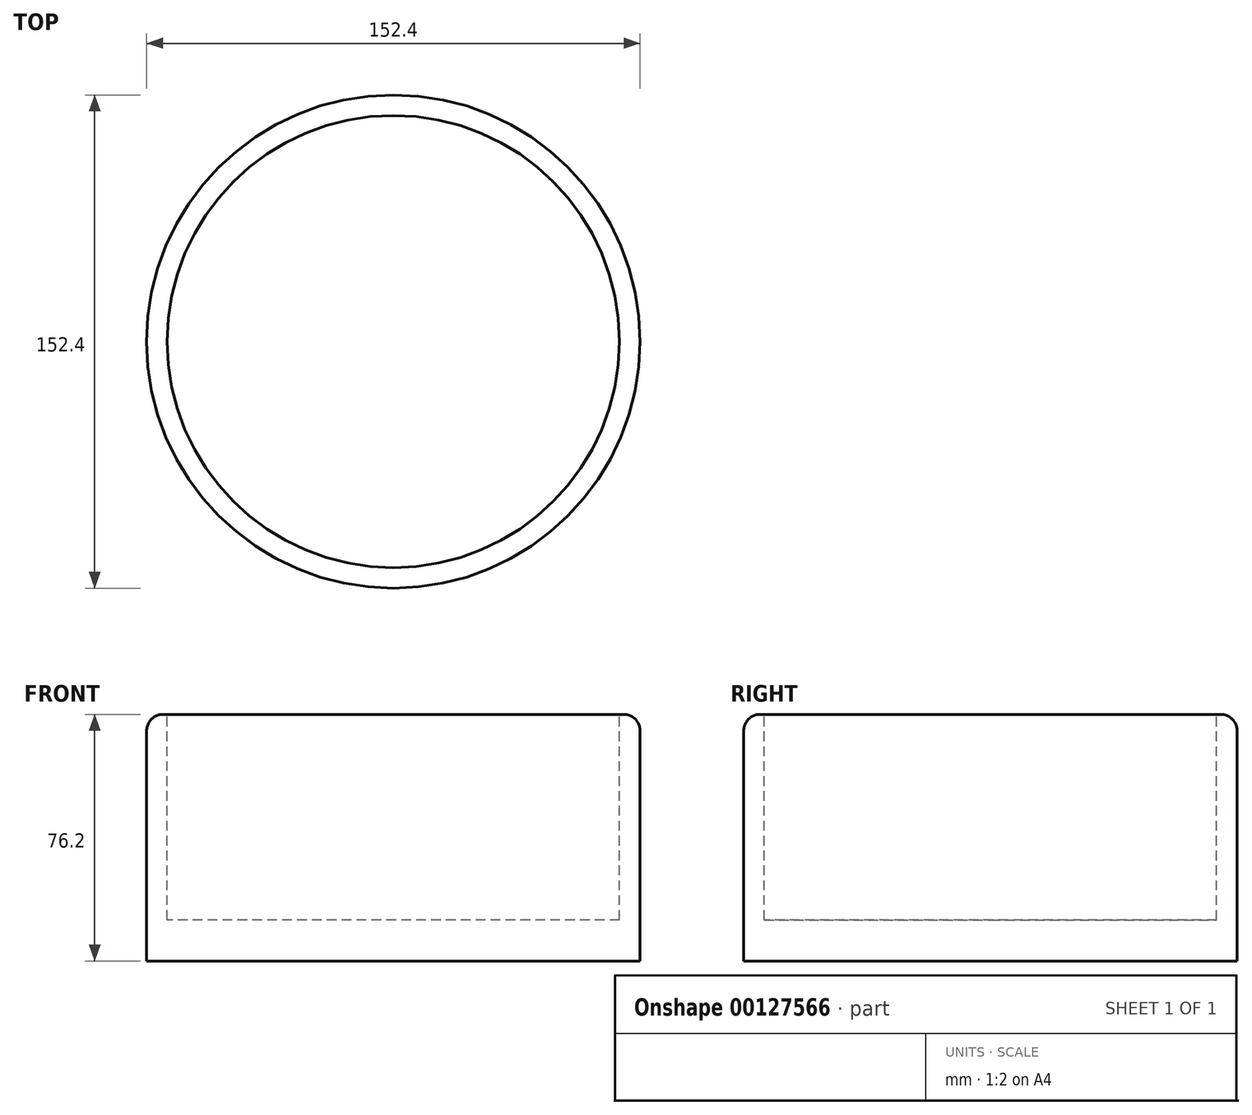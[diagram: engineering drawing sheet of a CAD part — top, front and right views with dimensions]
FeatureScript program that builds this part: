
annotation { "Feature Type Name" : "Feature", "Feature Type Description" : "" }
export const myFeature = defineFeature(function(context is Context, id is Id, definition is map)
    precondition{}
    {
        {
            var Q0;
            Q0=qCreatedBy(makeId("Front.planeOp"),FACE);
            var sketch = newSketch(context, id + "F0", { "sketchPlane" : qUnion([Q0])});
            skCircle(sketch, "E0.cCircle", {"center": v(0, 0) * mm, "radius": 38.1 * mm, "construction": true});
            skLineSegment(sketch, "E0.0", {"start": v(38.1, 38.1) * mm, "end": v(38.1, -38.1) * mm});
            skLineSegment(sketch, "E0.1", {"start": v(38.1, -38.1) * mm, "end": v(-38.1, -38.1) * mm});
            skLineSegment(sketch, "E0.2", {"start": v(-38.1, -38.1) * mm, "end": v(-38.1, 38.1) * mm});
            skLineSegment(sketch, "E0.3", {"start": v(-38.1, 38.1) * mm, "end": v(38.1, 38.1) * mm});
            skPoint(sketch, "E0.0.midPoint", {"position": v(38.1, 0) * mm});
            skSolve(sketch);
        }
        {
            var Q0;
            Q0 = qSketchRegion(id + "F0", true);
            var Q1;
            Q1=sQuery(id+"F0.wireOp",EDGE,"E0.0");
            revolve(context, id + "F1", {"entities" : qUnion([Q0]), "axis" : qUnion([Q1]), "revolveType" : RevolveType.FULL});
        }
        {
            var Q0;
            Q0=makeQuery(id+"F1.opRevolve","SWEPT_FACE",FACE,{"disambiguationData":[OSD([sQuery(id+"F0.wireOp",EDGE,"E0.3")])]});
            var sketch = newSketch(context, id + "F2", { "sketchPlane" : qUnion([Q0])});
            skCircle(sketch, "E1.0", {"center": v(38.1, 0) * mm, "radius": 69.85 * mm});
            skSolve(sketch);
        }
        {
            var Q0;
            Q0=makeQuery(id+"F2.imprint","IMPRINT",FACE,{"disambiguationData":[TD([[makeQuery(id+"F2.imprint","IMPRINT",EDGE,{"derivedFrom":sQuery(id+"F2.wireOp",EDGE,"E1.0")}),1.0]])]});
            extrude(context, id + "F3", {"entities" : qUnion([Q0]), "operationType" : NewBodyOperationType.REMOVE, "oppositeDirection" : true, "depth" : 63.5 * mm});
        }
        {
            var Q0;
            Q0=makeQuery(id+"F1.opRevolve","SWEPT_EDGE",EDGE,{"disambiguationData":[OSD([sQuery(id+"F0.wireOp",EDGE,"E0.2"),sQuery(id+"F0.wireOp",EDGE,"E0.3")])]});
            fillet(context, id + "F4", {"entities" : qUnion([Q0]), "radius" : 5.08 * mm, "tangentPropagation" : true, "allowEdgeOverflow" : false});
        }
    });
